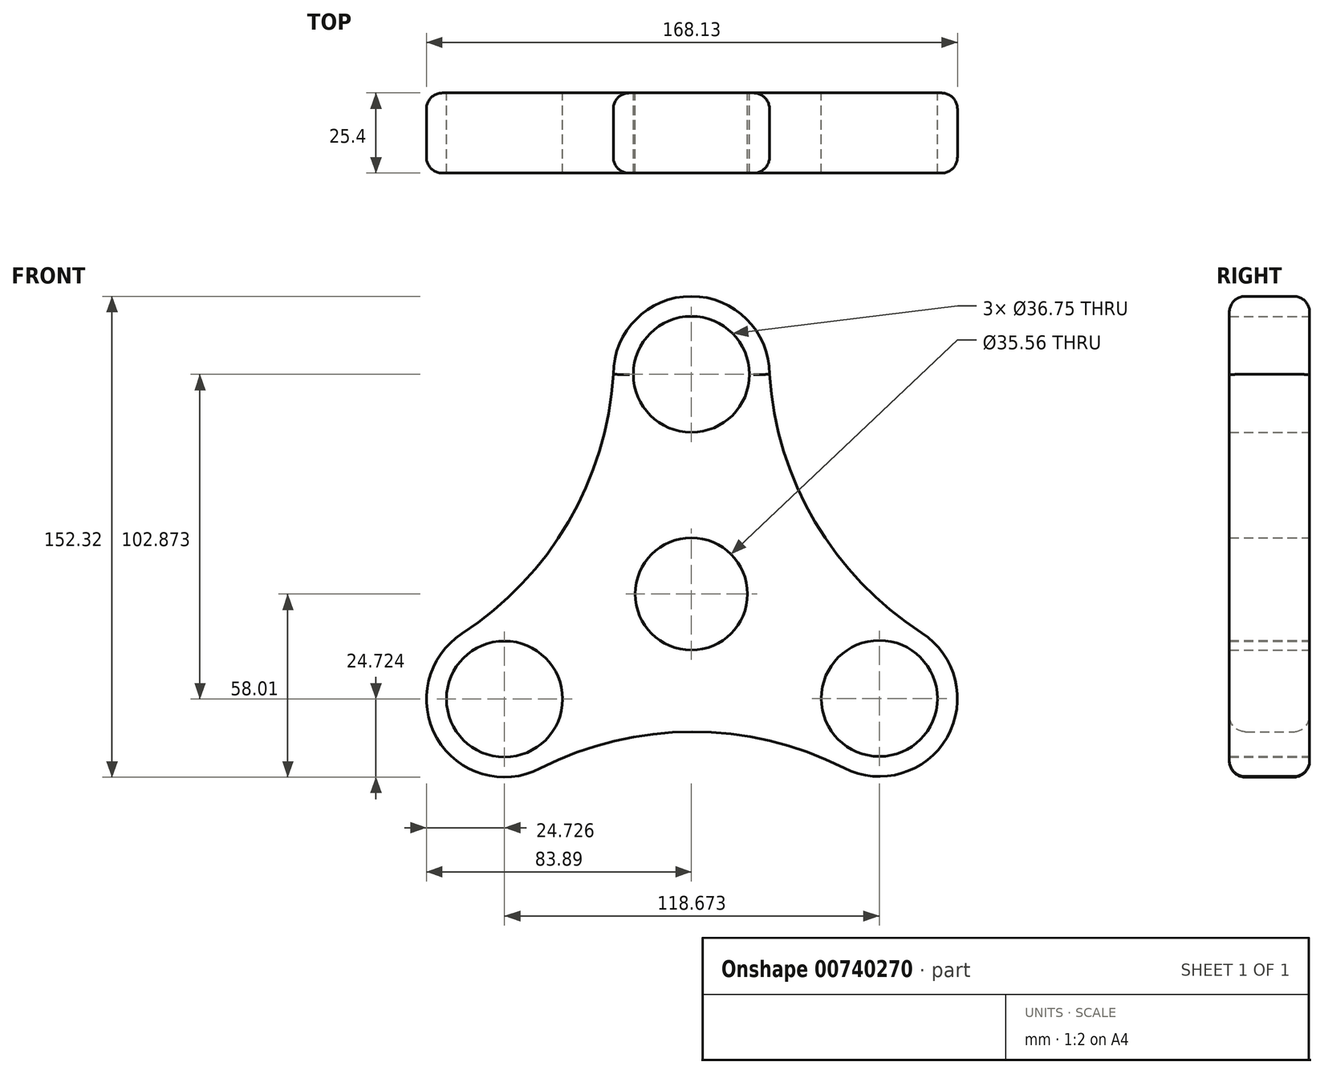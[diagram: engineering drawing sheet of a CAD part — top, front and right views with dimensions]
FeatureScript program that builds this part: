
annotation { "Feature Type Name" : "Feature", "Feature Type Description" : "" }
export const myFeature = defineFeature(function(context is Context, id is Id, definition is map)
    precondition{}
    {
        {
            var Q0;
            Q0=qCreatedBy(makeId("Front.planeOp"),FACE);
            var sketch = newSketch(context, id + "F0", { "sketchPlane" : qUnion([Q0])});
            skCircle(sketch, "E0", {"center": v(0, 0) * mm, "radius": 17.78 * mm});
            skCircle(sketch, "E1", {"center": v(0, 69.59) * mm, "radius": 18.38 * mm});
            skCircle(sketch, "E2.1.0", {"center": v(-59.16, -33.29) * mm, "radius": 18.38 * mm});
            skCircle(sketch, "E2.2.0", {"center": v(59.5, -33.09) * mm, "radius": 18.38 * mm});
            skPoint(sketch, "E2.center", {"position": v(0.11, 1.07) * mm});
            skCircle(sketch, "E3.0", {"center": v(0, 0) * mm, "radius": 24.13 * mm});
            skCircle(sketch, "E4.0", {"center": v(0, 69.59) * mm, "radius": 24.73 * mm});
            skCircle(sketch, "E5.0", {"center": v(59.5, -33.09) * mm, "radius": 24.73 * mm});
            skCircle(sketch, "E6.0", {"center": v(-59.16, -33.29) * mm, "radius": 24.73 * mm});
            skArc(sketch, "E7", {"start": v(-72.63, -12.55) * mm, "mid": v(-38.91, 22.82) * mm, "end": v(-24.73, 69.59) * mm});
            skArc(sketch, "E8", {"start": v(24.73, 69.59) * mm, "mid": v(39.09, 22.92) * mm, "end": v(72.9, -12.3) * mm});
            skArc(sketch, "E9", {"start": v(48.3, -55.12) * mm, "mid": v(0.19, -43.63) * mm, "end": v(-47.87, -55.28) * mm});
            skSolve(sketch);
        }
        {
            var Q0;
            Q0=makeQuery(id+"F0.imprint","IMPRINT",FACE,{"disambiguationData":[TD([[makeQuery(id+"F0.imprint","IMPRINT",EDGE,{"derivedFrom":sQuery(id+"F0.wireOp",EDGE,"E0")}),-1.0]])]});
            var Q1;
            Q1=makeQuery(id+"F0.imprint","IMPRINT",FACE,{"disambiguationData":[TD([[makeQuery(id+"F0.imprint","IMPRINT",EDGE,{"derivedFrom":sQuery(id+"F0.wireOp",EDGE,"E3.0")}),-1.0]])]});
            var Q2;
            Q2=makeQuery(id+"F0.imprint","IMPRINT",FACE,{"disambiguationData":[TD([[makeQuery(id+"F0.imprint","IMPRINT",EDGE,{"derivedFrom":sQuery(id+"F0.wireOp",EDGE,"E1")}),-1.0]])]});
            var Q3;
            Q3=makeQuery(id+"F0.imprint","IMPRINT",FACE,{"disambiguationData":[TD([[makeQuery(id+"F0.imprint","IMPRINT",EDGE,{"derivedFrom":sQuery(id+"F0.wireOp",EDGE,"E2.2.0")}),-1.0]])]});
            var Q4;
            Q4=makeQuery(id+"F0.imprint","IMPRINT",FACE,{"disambiguationData":[TD([[makeQuery(id+"F0.imprint","IMPRINT",EDGE,{"derivedFrom":sQuery(id+"F0.wireOp",EDGE,"E2.1.0")}),-1.0]])]});
            extrude(context, id + "F1", {"entities" : qUnion([Q0, Q1, Q2, Q3, Q4]), "depth" : 25.4 * mm, "offsetDistance" : 25.4 * mm});
        }
        {
            var Q0;
            Q0=makeQuery(id+"F1.opExtrude","CAP_EDGE",EDGE,{"disambiguationData":[OSD([sQuery(id+"F0.wireOp",EDGE,"E8")])],"isStart":false});
            var Q1;
            Q1=makeQuery(id+"F1.opExtrude","CAP_EDGE",EDGE,{"disambiguationData":[OSD([sQuery(id+"F0.wireOp",EDGE,"E8")])],"isStart":true});
            var Q2;
            Q2=makeQuery(id+"F1.opExtrude","CAP_EDGE",EDGE,{"disambiguationData":[OSD([sQuery(id+"F0.wireOp",EDGE,"E9")])],"isStart":false});
            var Q3;
            Q3=makeQuery(id+"F1.opExtrude","CAP_EDGE",EDGE,{"disambiguationData":[OSD([sQuery(id+"F0.wireOp",EDGE,"E7")])],"isStart":false});
            var Q4;
            Q4=makeQuery(id+"F1.opExtrude","CAP_EDGE",EDGE,{"disambiguationData":[OSD([sQuery(id+"F0.wireOp",EDGE,"E7")])],"isStart":true});
            var Q5;
            Q5=makeQuery(id+"F1.opExtrude","CAP_EDGE",EDGE,{"disambiguationData":[OSD([sQuery(id+"F0.wireOp",EDGE,"E9")])],"isStart":true});
            var Q6;
            Q6=makeQuery(id+"F1.opExtrude","CAP_EDGE",EDGE,{"disambiguationData":[OSD([sQuery(id+"F0.wireOp",EDGE,"E6.0")])],"isStart":false});
            var Q7;
            Q7=makeQuery(id+"F1.opExtrude","CAP_EDGE",EDGE,{"disambiguationData":[OSD([sQuery(id+"F0.wireOp",EDGE,"E6.0")])],"isStart":true});
            var Q8;
            Q8=makeQuery(id+"F1.opExtrude","CAP_EDGE",EDGE,{"disambiguationData":[OSD([sQuery(id+"F0.wireOp",EDGE,"E5.0")])],"isStart":false});
            var Q9;
            Q9=makeQuery(id+"F1.opExtrude","CAP_EDGE",EDGE,{"disambiguationData":[OSD([sQuery(id+"F0.wireOp",EDGE,"E5.0")])],"isStart":true});
            fillet(context, id + "F2", {"entities" : qUnion([Q0, Q1, Q2, Q3, Q4, Q5, Q6, Q7, Q8, Q9]), "radius" : 5.08 * mm, "tangentPropagation" : true, "allowEdgeOverflow" : false});
        }
        {
            var Q0;
            Q0=makeQuery(id+"F1.opExtrude","CAP_EDGE",EDGE,{"disambiguationData":[OSD([sQuery(id+"F0.wireOp",EDGE,"E4.0")])],"isStart":false});
            var Q1;
            Q1=makeQuery(id+"F1.opExtrude","CAP_EDGE",EDGE,{"disambiguationData":[OSD([sQuery(id+"F0.wireOp",EDGE,"E4.0")])],"isStart":true});
            fillet(context, id + "F3", {"entities" : qUnion([Q0, Q1]), "radius" : 5.08 * mm, "tangentPropagation" : true, "allowEdgeOverflow" : false});
        }
    });
